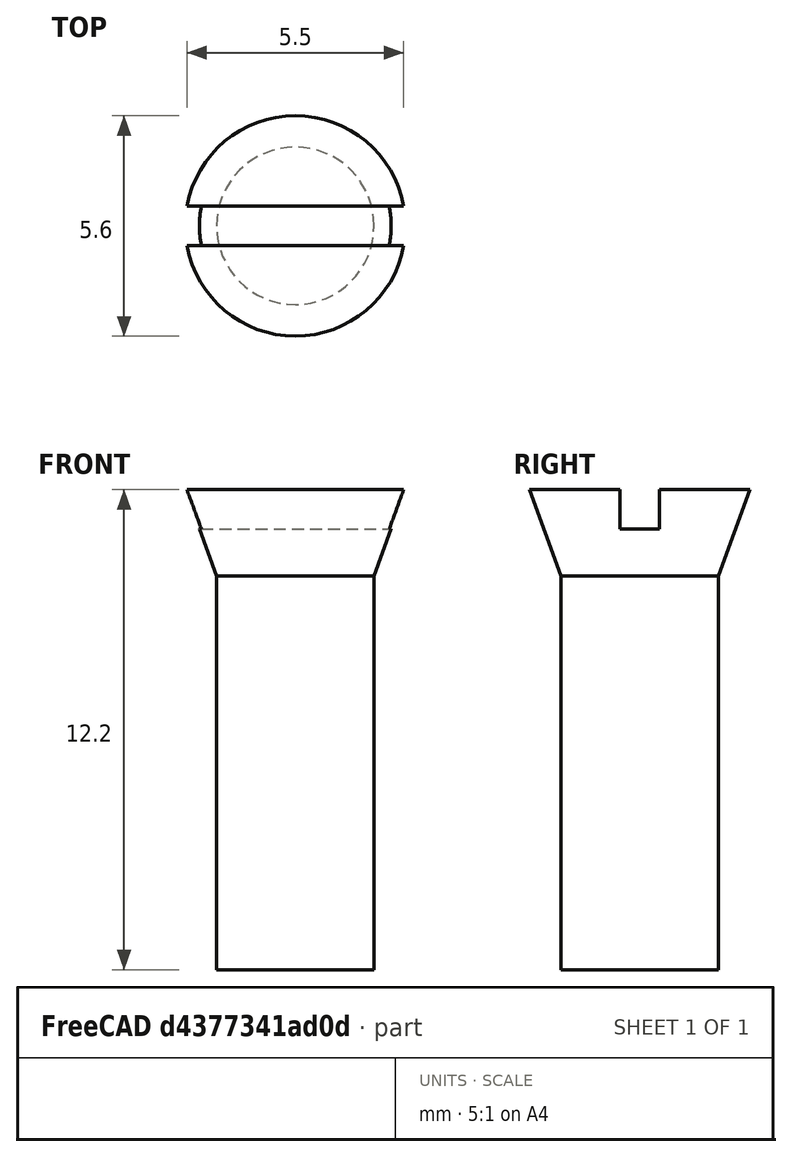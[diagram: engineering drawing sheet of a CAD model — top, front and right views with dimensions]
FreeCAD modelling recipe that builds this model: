
FCSTD DOCUMENT  (FreeCAD 0.21R33694 (Git))
Label: OJT1_T14R01_cargol
License: All rights reserved
LicenseURL: https://en.wikipedia.org/wiki/All_rights_reserved
objects: Part::Cylinder×1, Part::Cone×1, Part::MultiFuse×1, Part::Box×1, Part::Cut×1
note: 5 computed .brp shape members not serialized (recipe doc carries the construction recipe); baked Part::Feature solids carry a one-line shape summary decoded from their .brp

FEATURE [Part::Cylinder] Cylinder  label="Cilindre"
  Angle = 360
  AttacherType = Attacher::AttachEngine3D
  FirstAngle = 0
  Height = 10
  Radius = 2
  SecondAngle = 0
FEATURE [Part::Cone] Cone  label="Con"
  Angle = 360
  AttacherType = Attacher::AttachEngine3D
  Height = 2.2
  Placement = pos=(0,0,10) rot=(0,0,1;0rad)
  Radius1 = 2
  Radius2 = 2.8
FEATURE [Part::MultiFuse] Fusion
  Shapes = -> [Cylinder,Cone]
FEATURE [Part::Box] Box  label="Cub"
  AttacherType = Attacher::AttachEngine3D
  Height = 1
  Length = 6
  Placement = pos=(-3,-0.5,11.2) rot=(0,0,1;0rad)
  Width = 1
FEATURE [Part::Cut] Cut  label="Cargol"
  Base = -> Fusion
  Tool = -> Box
